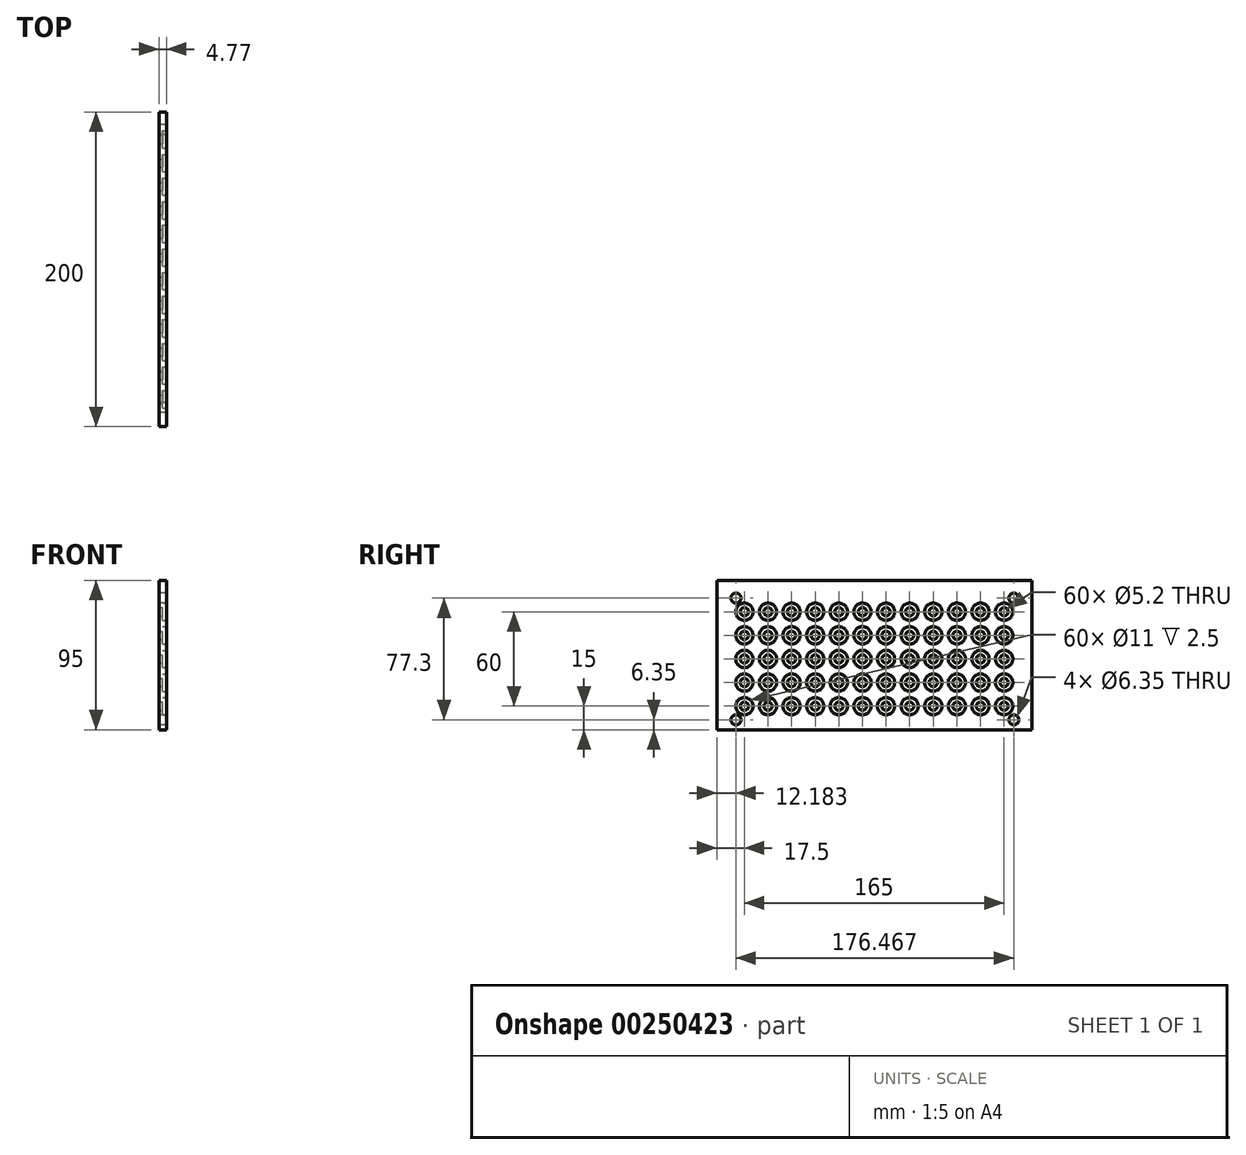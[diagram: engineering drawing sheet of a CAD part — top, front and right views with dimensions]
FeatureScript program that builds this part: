
annotation { "Feature Type Name" : "Feature", "Feature Type Description" : "" }
export const myFeature = defineFeature(function(context is Context, id is Id, definition is map)
    precondition{}
    {
        {
            var Q0;
            Q0=qCreatedBy(makeId("Right.planeOp"),FACE);
            var sketch = newSketch(context, id + "F0", { "sketchPlane" : qUnion([Q0])});
            skLineSegment(sketch, "E0.bottom", {"start": v(-100, 50) * mm, "end": v(100, 50) * mm, "construction": true});
            skLineSegment(sketch, "E0.top", {"start": v(-100, -50) * mm, "end": v(100, -50) * mm, "construction": true});
            skLineSegment(sketch, "E0.left", {"start": v(-100, 50) * mm, "end": v(-100, -45) * mm});
            skLineSegment(sketch, "E0.right", {"start": v(100, 50) * mm, "end": v(100, -45) * mm});
            skLineSegment(sketch, "E1", {"start": v(-100, -45) * mm, "end": v(100, -45) * mm});
            skCircle(sketch, "E2", {"center": v(-87.82, -38.65) * mm, "radius": 3.18 * mm});
            skCircle(sketch, "E3", {"center": v(-87.82, 38.65) * mm, "radius": 3.18 * mm});
            skCircle(sketch, "E4", {"center": v(88.65, 38.65) * mm, "radius": 3.18 * mm});
            skCircle(sketch, "E5", {"center": v(88.65, -38.65) * mm, "radius": 3.18 * mm});
            skLineSegment(sketch, "E6", {"start": v(-100, 45) * mm, "end": v(100, 45) * mm, "construction": true});
            skLineSegment(sketch, "E7", {"start": v(-95, 50) * mm, "end": v(-95, -45) * mm, "construction": true});
            skLineSegment(sketch, "E8", {"start": v(95, 50) * mm, "end": v(95, -45) * mm, "construction": true});
            skLineSegment(sketch, "E9", {"start": v(-100, 50) * mm, "end": v(100, 50) * mm});
            skSolve(sketch);
        }
        {
            var Q0;
            Q0=makeQuery(id+"F0.imprint","IMPRINT",FACE,{"disambiguationData":[TD([[makeQuery(id+"F0.imprint","IMPRINT",EDGE,{"derivedFrom":sQuery(id+"F0.wireOp",EDGE,"E0.left")}),1.0]])]});
            extrude(context, id + "F1", {"entities" : qUnion([Q0]), "depth" : 4.77 * mm});
        }
        {
            var Q0;
            Q0=makeQuery(id+"F1.opExtrude","CAP_FACE",FACE,{"disambiguationData":[OSD([sQuery(id+"F0.wireOp",EDGE,"E0.left"),sQuery(id+"F0.wireOp",EDGE,"E0.right"),sQuery(id+"F0.wireOp",EDGE,"E1"),sQuery(id+"F0.wireOp",EDGE,"E2"),sQuery(id+"F0.wireOp",EDGE,"E3"),sQuery(id+"F0.wireOp",EDGE,"E4"),sQuery(id+"F0.wireOp",EDGE,"E5"),sQuery(id+"F0.wireOp",EDGE,"E9")])],"isStart":false});
            var sketch = newSketch(context, id + "F2", { "sketchPlane" : qUnion([Q0])});
            skCircle(sketch, "E10", {"center": v(-82.5, 30) * mm, "radius": 2.6 * mm});
            skCircle(sketch, "E11.0.1.0", {"center": v(-82.5, 15) * mm, "radius": 2.6 * mm});
            skCircle(sketch, "E11.0.2.0", {"center": v(-82.5, 0) * mm, "radius": 2.6 * mm});
            skCircle(sketch, "E11.0.3.0", {"center": v(-82.5, -15) * mm, "radius": 2.6 * mm});
            skCircle(sketch, "E11.1.0.0", {"center": v(-67.5, 30) * mm, "radius": 2.6 * mm});
            skCircle(sketch, "E11.1.1.0", {"center": v(-67.5, 15) * mm, "radius": 2.6 * mm});
            skCircle(sketch, "E11.1.2.0", {"center": v(-67.5, 0) * mm, "radius": 2.6 * mm});
            skCircle(sketch, "E11.1.3.0", {"center": v(-67.5, -15) * mm, "radius": 2.6 * mm});
            skCircle(sketch, "E11.2.0.0", {"center": v(-52.5, 30) * mm, "radius": 2.6 * mm});
            skCircle(sketch, "E11.2.1.0", {"center": v(-52.5, 15) * mm, "radius": 2.6 * mm});
            skCircle(sketch, "E11.2.2.0", {"center": v(-52.5, 0) * mm, "radius": 2.6 * mm});
            skCircle(sketch, "E11.2.3.0", {"center": v(-52.5, -15) * mm, "radius": 2.6 * mm});
            skCircle(sketch, "E11.3.0.0", {"center": v(-37.5, 30) * mm, "radius": 2.6 * mm});
            skCircle(sketch, "E11.3.1.0", {"center": v(-37.5, 15) * mm, "radius": 2.6 * mm});
            skCircle(sketch, "E11.3.2.0", {"center": v(-37.5, 0) * mm, "radius": 2.6 * mm});
            skCircle(sketch, "E11.3.3.0", {"center": v(-37.5, -15) * mm, "radius": 2.6 * mm});
            skCircle(sketch, "E11.4.0.0", {"center": v(-22.5, 30) * mm, "radius": 2.6 * mm});
            skCircle(sketch, "E11.4.1.0", {"center": v(-22.5, 15) * mm, "radius": 2.6 * mm});
            skCircle(sketch, "E11.4.2.0", {"center": v(-22.5, 0) * mm, "radius": 2.6 * mm});
            skCircle(sketch, "E11.4.3.0", {"center": v(-22.5, -15) * mm, "radius": 2.6 * mm});
            skCircle(sketch, "E11.5.0.0", {"center": v(-7.5, 30) * mm, "radius": 2.6 * mm});
            skCircle(sketch, "E11.5.1.0", {"center": v(-7.5, 15) * mm, "radius": 2.6 * mm});
            skCircle(sketch, "E11.5.2.0", {"center": v(-7.5, 0) * mm, "radius": 2.6 * mm});
            skCircle(sketch, "E11.5.3.0", {"center": v(-7.5, -15) * mm, "radius": 2.6 * mm});
            skCircle(sketch, "E11.6.0.0", {"center": v(7.5, 30) * mm, "radius": 2.6 * mm});
            skCircle(sketch, "E11.6.1.0", {"center": v(7.5, 15) * mm, "radius": 2.6 * mm});
            skCircle(sketch, "E11.6.2.0", {"center": v(7.5, 0) * mm, "radius": 2.6 * mm});
            skCircle(sketch, "E11.6.3.0", {"center": v(7.5, -15) * mm, "radius": 2.6 * mm});
            skCircle(sketch, "E11.7.0.0", {"center": v(22.5, 30) * mm, "radius": 2.6 * mm});
            skCircle(sketch, "E11.7.1.0", {"center": v(22.5, 15) * mm, "radius": 2.6 * mm});
            skCircle(sketch, "E11.7.2.0", {"center": v(22.5, 0) * mm, "radius": 2.6 * mm});
            skCircle(sketch, "E11.7.3.0", {"center": v(22.5, -15) * mm, "radius": 2.6 * mm});
            skCircle(sketch, "E11.8.0.0", {"center": v(37.5, 30) * mm, "radius": 2.6 * mm});
            skCircle(sketch, "E11.8.1.0", {"center": v(37.5, 15) * mm, "radius": 2.6 * mm});
            skCircle(sketch, "E11.8.2.0", {"center": v(37.5, 0) * mm, "radius": 2.6 * mm});
            skCircle(sketch, "E11.8.3.0", {"center": v(37.5, -15) * mm, "radius": 2.6 * mm});
            skLineSegment(sketch, "E11.direction1", {"start": v(-82.5, 30) * mm, "end": v(-67.5, 30) * mm, "construction": true});
            skLineSegment(sketch, "E11.direction2", {"start": v(-82.5, 30) * mm, "end": v(-82.5, 15) * mm, "construction": true});
            skCircle(sketch, "E12.0.9.0", {"center": v(52.5, 30) * mm, "radius": 2.6 * mm});
            skCircle(sketch, "E12.0.9.1", {"center": v(52.5, 15) * mm, "radius": 2.6 * mm});
            skCircle(sketch, "E12.0.9.2", {"center": v(52.5, 0) * mm, "radius": 2.6 * mm});
            skCircle(sketch, "E12.0.9.3", {"center": v(52.5, -15) * mm, "radius": 2.6 * mm});
            skCircle(sketch, "E12.0.10.0", {"center": v(67.5, 30) * mm, "radius": 2.6 * mm});
            skCircle(sketch, "E12.0.10.1", {"center": v(67.5, 15) * mm, "radius": 2.6 * mm});
            skCircle(sketch, "E12.0.10.2", {"center": v(67.5, 0) * mm, "radius": 2.6 * mm});
            skCircle(sketch, "E12.0.10.3", {"center": v(67.5, -15) * mm, "radius": 2.6 * mm});
            skCircle(sketch, "E12.0.11.0", {"center": v(82.5, 30) * mm, "radius": 2.6 * mm});
            skCircle(sketch, "E12.0.11.1", {"center": v(82.5, 15) * mm, "radius": 2.6 * mm});
            skCircle(sketch, "E12.0.11.2", {"center": v(82.5, 0) * mm, "radius": 2.6 * mm});
            skCircle(sketch, "E12.0.11.3", {"center": v(82.5, -15) * mm, "radius": 2.6 * mm});
            skCircle(sketch, "E13.0.0.4", {"center": v(-82.5, -30) * mm, "radius": 2.6 * mm});
            skCircle(sketch, "E13.0.1.4", {"center": v(-67.5, -30) * mm, "radius": 2.6 * mm});
            skCircle(sketch, "E13.0.2.4", {"center": v(-52.5, -30) * mm, "radius": 2.6 * mm});
            skCircle(sketch, "E13.0.3.4", {"center": v(-37.5, -30) * mm, "radius": 2.6 * mm});
            skCircle(sketch, "E13.0.4.4", {"center": v(-22.5, -30) * mm, "radius": 2.6 * mm});
            skCircle(sketch, "E13.0.5.4", {"center": v(-7.5, -30) * mm, "radius": 2.6 * mm});
            skCircle(sketch, "E13.0.6.4", {"center": v(7.5, -30) * mm, "radius": 2.6 * mm});
            skCircle(sketch, "E13.0.7.4", {"center": v(22.5, -30) * mm, "radius": 2.6 * mm});
            skCircle(sketch, "E13.0.8.4", {"center": v(37.5, -30) * mm, "radius": 2.6 * mm});
            skCircle(sketch, "E13.0.9.4", {"center": v(52.5, -30) * mm, "radius": 2.6 * mm});
            skCircle(sketch, "E13.0.10.4", {"center": v(67.5, -30) * mm, "radius": 2.6 * mm});
            skCircle(sketch, "E13.0.11.4", {"center": v(82.5, -30) * mm, "radius": 2.6 * mm});
            skSolve(sketch);
        }
        {
            var Q0;
            Q0 = qSketchRegion(id + "F2", true);
            extrude(context, id + "F3", {"entities" : qUnion([Q0]), "operationType" : NewBodyOperationType.REMOVE, "endBound" : BoundingType.UP_TO_NEXT, "oppositeDirection" : true, "depth" : 25 * mm});
        }
        {
            var Q0;
            Q0=makeQuery(id+"F1.opExtrude","CAP_FACE",FACE,{"disambiguationData":[OSD([sQuery(id+"F0.wireOp",EDGE,"E0.left"),sQuery(id+"F0.wireOp",EDGE,"E0.right"),sQuery(id+"F0.wireOp",EDGE,"E1"),sQuery(id+"F0.wireOp",EDGE,"E2"),sQuery(id+"F0.wireOp",EDGE,"E3"),sQuery(id+"F0.wireOp",EDGE,"E4"),sQuery(id+"F0.wireOp",EDGE,"E5"),sQuery(id+"F0.wireOp",EDGE,"E9")])],"isStart":false});
            var sketch = newSketch(context, id + "F4", { "sketchPlane" : qUnion([Q0])});
            skCircle(sketch, "E14", {"center": v(-82.5, 30) * mm, "radius": 5.5 * mm});
            skCircle(sketch, "E15.0.1.0", {"center": v(-82.5, 15) * mm, "radius": 5.5 * mm});
            skCircle(sketch, "E15.0.2.0", {"center": v(-82.5, 0) * mm, "radius": 5.5 * mm});
            skCircle(sketch, "E15.0.3.0", {"center": v(-82.5, -15) * mm, "radius": 5.5 * mm});
            skCircle(sketch, "E15.1.0.0", {"center": v(-67.5, 30) * mm, "radius": 5.5 * mm});
            skCircle(sketch, "E15.1.1.0", {"center": v(-67.5, 15) * mm, "radius": 5.5 * mm});
            skCircle(sketch, "E15.1.2.0", {"center": v(-67.5, 0) * mm, "radius": 5.5 * mm});
            skCircle(sketch, "E15.1.3.0", {"center": v(-67.5, -15) * mm, "radius": 5.5 * mm});
            skCircle(sketch, "E15.2.0.0", {"center": v(-52.5, 30) * mm, "radius": 5.5 * mm});
            skCircle(sketch, "E15.2.1.0", {"center": v(-52.5, 15) * mm, "radius": 5.5 * mm});
            skCircle(sketch, "E15.2.2.0", {"center": v(-52.5, 0) * mm, "radius": 5.5 * mm});
            skCircle(sketch, "E15.2.3.0", {"center": v(-52.5, -15) * mm, "radius": 5.5 * mm});
            skCircle(sketch, "E15.3.0.0", {"center": v(-37.5, 30) * mm, "radius": 5.5 * mm});
            skCircle(sketch, "E15.3.1.0", {"center": v(-37.5, 15) * mm, "radius": 5.5 * mm});
            skCircle(sketch, "E15.3.2.0", {"center": v(-37.5, 0) * mm, "radius": 5.5 * mm});
            skCircle(sketch, "E15.3.3.0", {"center": v(-37.5, -15) * mm, "radius": 5.5 * mm});
            skCircle(sketch, "E15.4.0.0", {"center": v(-22.5, 30) * mm, "radius": 5.5 * mm});
            skCircle(sketch, "E15.4.1.0", {"center": v(-22.5, 15) * mm, "radius": 5.5 * mm});
            skCircle(sketch, "E15.4.2.0", {"center": v(-22.5, 0) * mm, "radius": 5.5 * mm});
            skCircle(sketch, "E15.4.3.0", {"center": v(-22.5, -15) * mm, "radius": 5.5 * mm});
            skCircle(sketch, "E15.5.0.0", {"center": v(-7.5, 30) * mm, "radius": 5.5 * mm});
            skCircle(sketch, "E15.5.1.0", {"center": v(-7.5, 15) * mm, "radius": 5.5 * mm});
            skCircle(sketch, "E15.5.2.0", {"center": v(-7.5, 0) * mm, "radius": 5.5 * mm});
            skCircle(sketch, "E15.5.3.0", {"center": v(-7.5, -15) * mm, "radius": 5.5 * mm});
            skCircle(sketch, "E15.6.0.0", {"center": v(7.5, 30) * mm, "radius": 5.5 * mm});
            skCircle(sketch, "E15.6.1.0", {"center": v(7.5, 15) * mm, "radius": 5.5 * mm});
            skCircle(sketch, "E15.6.2.0", {"center": v(7.5, 0) * mm, "radius": 5.5 * mm});
            skCircle(sketch, "E15.6.3.0", {"center": v(7.5, -15) * mm, "radius": 5.5 * mm});
            skCircle(sketch, "E15.7.0.0", {"center": v(22.5, 30) * mm, "radius": 5.5 * mm});
            skCircle(sketch, "E15.7.1.0", {"center": v(22.5, 15) * mm, "radius": 5.5 * mm});
            skCircle(sketch, "E15.7.2.0", {"center": v(22.5, 0) * mm, "radius": 5.5 * mm});
            skCircle(sketch, "E15.7.3.0", {"center": v(22.5, -15) * mm, "radius": 5.5 * mm});
            skCircle(sketch, "E15.8.0.0", {"center": v(37.5, 30) * mm, "radius": 5.5 * mm});
            skCircle(sketch, "E15.8.1.0", {"center": v(37.5, 15) * mm, "radius": 5.5 * mm});
            skCircle(sketch, "E15.8.2.0", {"center": v(37.5, 0) * mm, "radius": 5.5 * mm});
            skCircle(sketch, "E15.8.3.0", {"center": v(37.5, -15) * mm, "radius": 5.5 * mm});
            skLineSegment(sketch, "E15.direction1", {"start": v(-82.5, 30) * mm, "end": v(-67.5, 30) * mm, "construction": true});
            skLineSegment(sketch, "E15.direction2", {"start": v(-82.5, 30) * mm, "end": v(-82.5, 15) * mm, "construction": true});
            skCircle(sketch, "E16.0.0.4", {"center": v(-82.5, -30) * mm, "radius": 5.5 * mm});
            skCircle(sketch, "E16.0.1.4", {"center": v(-67.5, -30) * mm, "radius": 5.5 * mm});
            skCircle(sketch, "E16.0.2.4", {"center": v(-52.5, -30) * mm, "radius": 5.5 * mm});
            skCircle(sketch, "E16.0.3.4", {"center": v(-37.5, -30) * mm, "radius": 5.5 * mm});
            skCircle(sketch, "E16.0.4.4", {"center": v(-22.5, -30) * mm, "radius": 5.5 * mm});
            skCircle(sketch, "E16.0.5.4", {"center": v(-7.5, -30) * mm, "radius": 5.5 * mm});
            skCircle(sketch, "E16.0.6.4", {"center": v(7.5, -30) * mm, "radius": 5.5 * mm});
            skCircle(sketch, "E16.0.7.4", {"center": v(22.5, -30) * mm, "radius": 5.5 * mm});
            skCircle(sketch, "E16.0.8.4", {"center": v(37.5, -30) * mm, "radius": 5.5 * mm});
            skCircle(sketch, "E17.0.9.0", {"center": v(52.5, 30) * mm, "radius": 5.5 * mm});
            skCircle(sketch, "E17.0.9.1", {"center": v(52.5, 15) * mm, "radius": 5.5 * mm});
            skCircle(sketch, "E17.0.9.2", {"center": v(52.5, 0) * mm, "radius": 5.5 * mm});
            skCircle(sketch, "E17.0.9.3", {"center": v(52.5, -15) * mm, "radius": 5.5 * mm});
            skCircle(sketch, "E17.0.9.4", {"center": v(52.5, -30) * mm, "radius": 5.5 * mm});
            skCircle(sketch, "E17.0.10.0", {"center": v(67.5, 30) * mm, "radius": 5.5 * mm});
            skCircle(sketch, "E17.0.10.1", {"center": v(67.5, 15) * mm, "radius": 5.5 * mm});
            skCircle(sketch, "E17.0.10.2", {"center": v(67.5, 0) * mm, "radius": 5.5 * mm});
            skCircle(sketch, "E17.0.10.3", {"center": v(67.5, -15) * mm, "radius": 5.5 * mm});
            skCircle(sketch, "E17.0.10.4", {"center": v(67.5, -30) * mm, "radius": 5.5 * mm});
            skCircle(sketch, "E17.0.11.0", {"center": v(82.5, 30) * mm, "radius": 5.5 * mm});
            skCircle(sketch, "E17.0.11.1", {"center": v(82.5, 15) * mm, "radius": 5.5 * mm});
            skCircle(sketch, "E17.0.11.2", {"center": v(82.5, 0) * mm, "radius": 5.5 * mm});
            skCircle(sketch, "E17.0.11.3", {"center": v(82.5, -15) * mm, "radius": 5.5 * mm});
            skCircle(sketch, "E17.0.11.4", {"center": v(82.5, -30) * mm, "radius": 5.5 * mm});
            skSolve(sketch);
        }
        {
            var Q0;
            Q0 = qSketchRegion(id + "F4", true);
            extrude(context, id + "F5", {"entities" : qUnion([Q0]), "operationType" : NewBodyOperationType.REMOVE, "oppositeDirection" : true, "depth" : 2.5 * mm});
        }
    });
